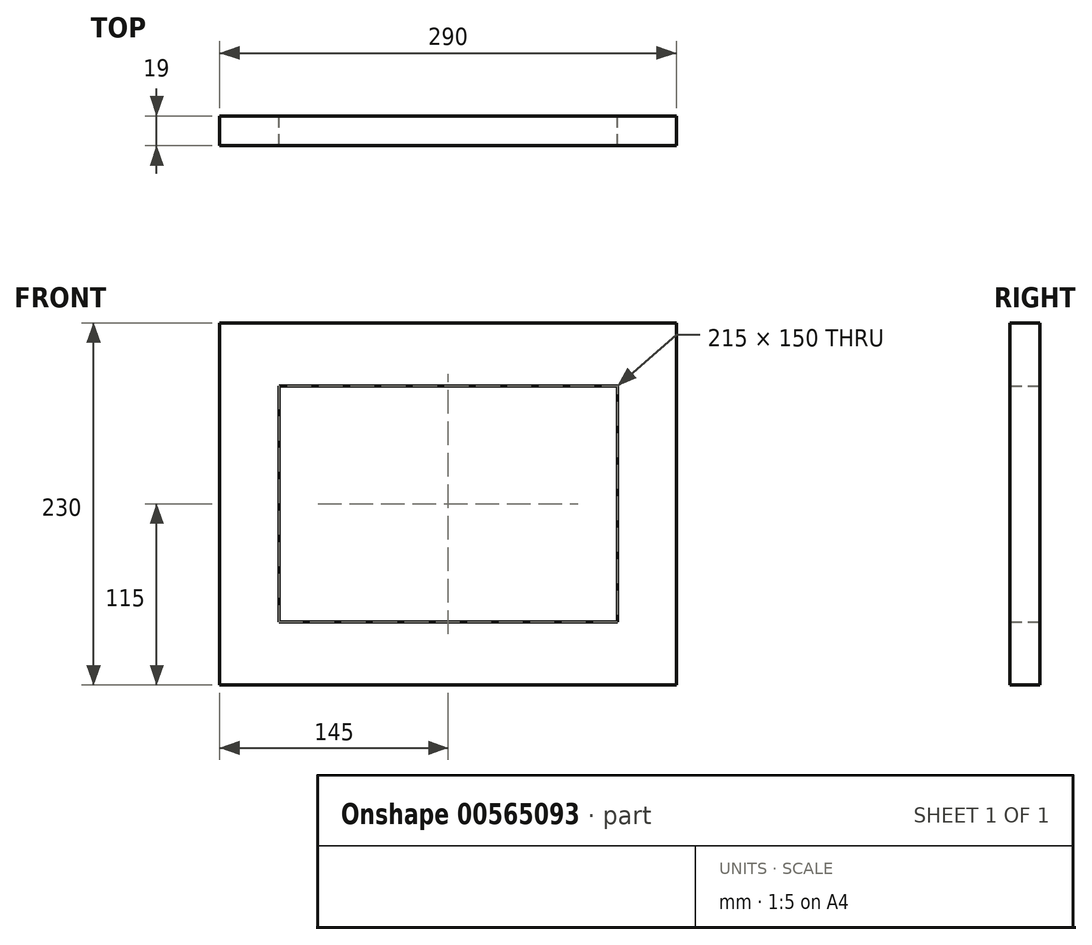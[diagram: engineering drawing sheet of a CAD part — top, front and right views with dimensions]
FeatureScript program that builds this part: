
annotation { "Feature Type Name" : "Feature", "Feature Type Description" : "" }
export const myFeature = defineFeature(function(context is Context, id is Id, definition is map)
    precondition{}
    {
        {
            var Q0;
            Q0=qCreatedBy(makeId("Front.planeOp"),FACE);
            var sketch = newSketch(context, id + "F0", { "sketchPlane" : qUnion([Q0])});
            skLineSegment(sketch, "E0.bottom", {"start": v(-145, -115) * mm, "end": v(145, -115) * mm});
            skLineSegment(sketch, "E0.top", {"start": v(-145, 115) * mm, "end": v(145, 115) * mm});
            skLineSegment(sketch, "E0.left", {"start": v(-145, -115) * mm, "end": v(-145, 115) * mm});
            skLineSegment(sketch, "E0.right", {"start": v(145, -115) * mm, "end": v(145, 115) * mm});
            skSolve(sketch);
        }
        {
            var Q0;
            Q0=makeQuery(id+"F0.imprint","IMPRINT",FACE,{"disambiguationData":[TD([[makeQuery(id+"F0.imprint","IMPRINT",EDGE,{"derivedFrom":sQuery(id+"F0.wireOp",EDGE,"E0.bottom")}),1.0]])]});
            var sketch = newSketch(context, id + "F1", { "sketchPlane" : qUnion([Q0])});
            skLineSegment(sketch, "E1.bottom", {"start": v(107.5, 75) * mm, "end": v(-107.5, 75) * mm});
            skLineSegment(sketch, "E1.top", {"start": v(107.5, -75) * mm, "end": v(-107.5, -75) * mm});
            skLineSegment(sketch, "E1.left", {"start": v(107.5, 75) * mm, "end": v(107.5, -75) * mm});
            skLineSegment(sketch, "E1.right", {"start": v(-107.5, 75) * mm, "end": v(-107.5, -75) * mm});
            skSolve(sketch);
        }
        {
            var Q0;
            Q0=makeQuery(id+"F0.imprint","IMPRINT",FACE,{"disambiguationData":[TD([[makeQuery(id+"F0.imprint","IMPRINT",EDGE,{"derivedFrom":sQuery(id+"F0.wireOp",EDGE,"E0.bottom")}),1.0]])]});
            var Q1;
            Q1=sQuery(id+"F0.wireOp",EDGE,"E0.left");
            var Q2;
            Q2=sQuery(id+"F0.wireOp",EDGE,"E0.top");
            var Q3;
            Q3=sQuery(id+"F0.wireOp",EDGE,"E0.bottom");
            var Q4;
            Q4=sQuery(id+"F1.wireOp",EDGE,"E1.top");
            var Q5;
            Q5=sQuery(id+"F1.wireOp",EDGE,"E1.right");
            var Q6;
            Q6=sQuery(id+"F1.wireOp",EDGE,"E1.bottom");
            extrude(context, id + "F2", {"entities" : qUnion([Q0]), "surfaceEntities" : qUnion([Q1, Q2, Q3, Q4, Q5, Q6]), "depth" : 19 * mm, "offsetDistance" : 25 * mm});
        }
        {
            var Q0;
            Q0 = qSketchRegion(id + "F1", true);
            extrude(context, id + "F3", {"entities" : qUnion([Q0]), "operationType" : NewBodyOperationType.REMOVE, "depth" : 25 * mm, "offsetDistance" : 25 * mm});
        }
    });
